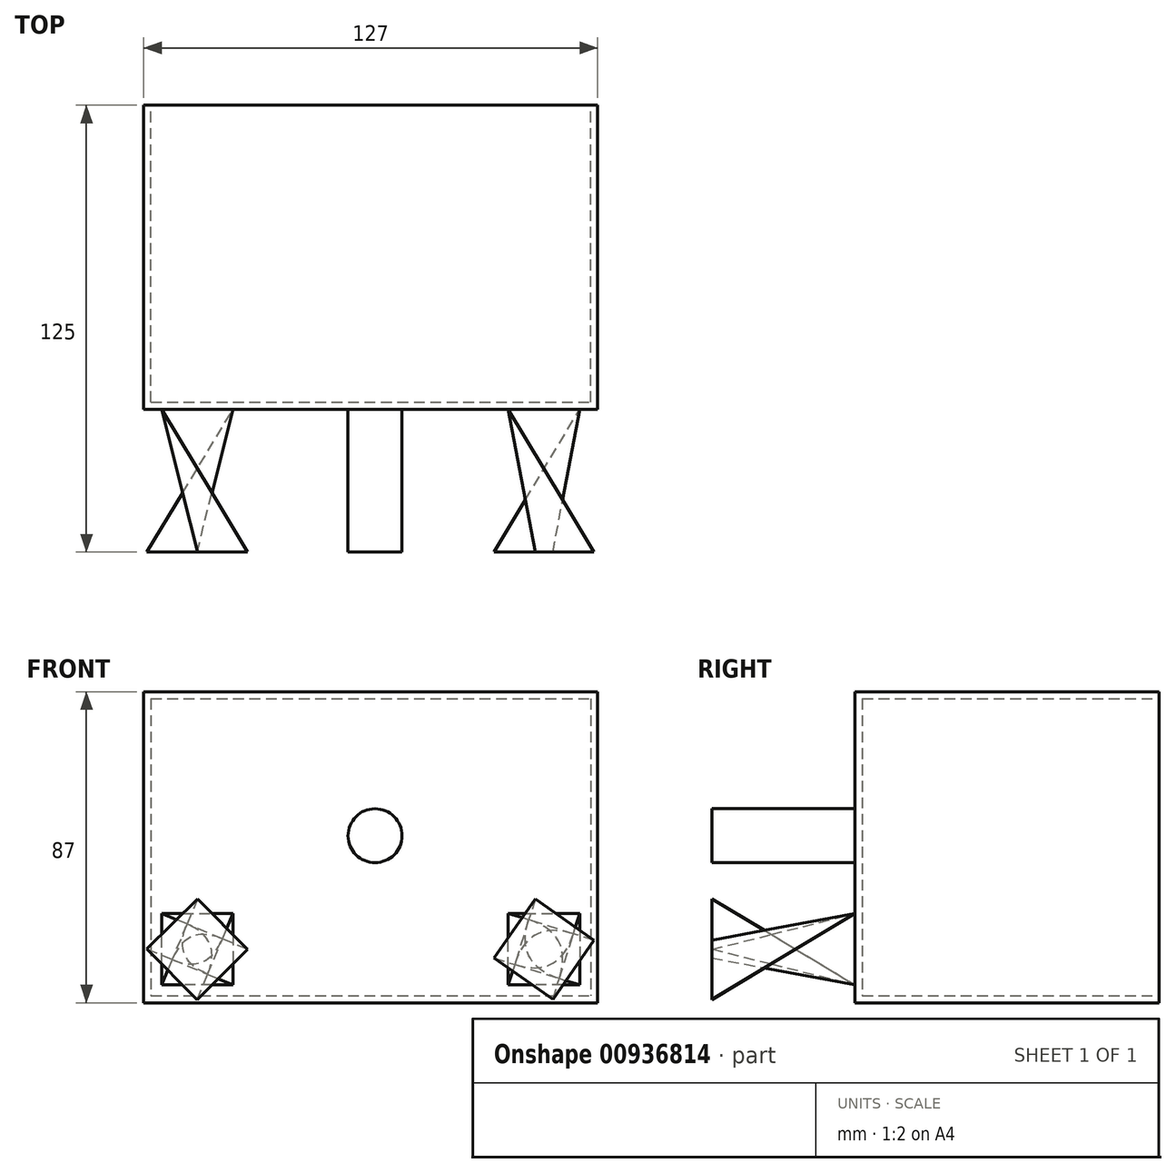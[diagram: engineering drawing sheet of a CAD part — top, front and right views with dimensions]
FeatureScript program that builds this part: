
annotation { "Feature Type Name" : "Feature", "Feature Type Description" : "" }
export const myFeature = defineFeature(function(context is Context, id is Id, definition is map)
    precondition{}
    {
        {
            var Q0;
            Q0=qCreatedBy(makeId("Front.planeOp"),FACE);
            var sketch = newSketch(context, id + "F0", { "sketchPlane" : qUnion([Q0])});
            skLineSegment(sketch, "E0.bottom", {"start": v(-53.91, 27.97) * mm, "end": v(73.09, 27.97) * mm});
            skLineSegment(sketch, "E0.top", {"start": v(-53.91, -59.03) * mm, "end": v(73.09, -59.03) * mm});
            skLineSegment(sketch, "E0.left", {"start": v(-53.91, 27.97) * mm, "end": v(-53.91, -59.03) * mm});
            skLineSegment(sketch, "E0.right", {"start": v(73.09, 27.97) * mm, "end": v(73.09, -59.03) * mm});
            skSolve(sketch);
        }
        {
            var Q0;
            Q0 = qSketchRegion(id + "F0", true);
            extrude(context, id + "F1", {"entities" : qUnion([Q0]), "depth" : 85 * mm, "offsetDistance" : 25 * mm});
        }
        {
            var Q0;
            Q0=makeQuery(id+"F1.opExtrude","CAP_FACE",FACE,{"disambiguationData":[OSD([sQuery(id+"F0.wireOp",EDGE,"E0.bottom"),sQuery(id+"F0.wireOp",EDGE,"E0.top"),sQuery(id+"F0.wireOp",EDGE,"E0.left"),sQuery(id+"F0.wireOp",EDGE,"E0.right")])],"isStart":true});
            shell(context, id + "F2", {"entities" : qUnion([Q0]), "thickness" : 2 * mm});
        }
        {
            var Q0;
            Q0=makeQuery(id+"F1.opExtrude","CAP_FACE",FACE,{"disambiguationData":[OSD([sQuery(id+"F0.wireOp",EDGE,"E0.bottom"),sQuery(id+"F0.wireOp",EDGE,"E0.top"),sQuery(id+"F0.wireOp",EDGE,"E0.left"),sQuery(id+"F0.wireOp",EDGE,"E0.right")])],"isStart":false});
            var sketch = newSketch(context, id + "F3", { "sketchPlane" : qUnion([Q0])});
            skCircle(sketch, "E1.cCircle", {"center": v(58.09, -44.03) * mm, "radius": 10 * mm, "construction": true});
            skLineSegment(sketch, "E1.0", {"start": v(68.09, -34.03) * mm, "end": v(68.09, -54.03) * mm});
            skLineSegment(sketch, "E1.1", {"start": v(68.09, -54.03) * mm, "end": v(48.09, -54.03) * mm});
            skLineSegment(sketch, "E1.2", {"start": v(48.09, -54.03) * mm, "end": v(48.09, -34.03) * mm});
            skLineSegment(sketch, "E1.3", {"start": v(48.09, -34.03) * mm, "end": v(68.09, -34.03) * mm});
            skPoint(sketch, "E1.0.midPoint", {"position": v(68.09, -44.03) * mm});
            skCircle(sketch, "E2.cCircle", {"center": v(-38.91, -44.03) * mm, "radius": 10 * mm, "construction": true});
            skLineSegment(sketch, "E2.0", {"start": v(-28.91, -54.03) * mm, "end": v(-48.91, -54.03) * mm});
            skLineSegment(sketch, "E2.1", {"start": v(-48.91, -54.03) * mm, "end": v(-48.91, -34.03) * mm});
            skLineSegment(sketch, "E2.2", {"start": v(-48.91, -34.03) * mm, "end": v(-28.91, -34.03) * mm});
            skLineSegment(sketch, "E2.3", {"start": v(-28.91, -34.03) * mm, "end": v(-28.91, -54.03) * mm});
            skPoint(sketch, "E2.0.midPoint", {"position": v(-38.91, -54.03) * mm});
            skCircle(sketch, "E3", {"center": v(10.8, -12.31) * mm, "radius": 7.55 * mm});
            skSolve(sketch);
        }
        {
            var Q0;
            Q0=makeQuery(id+"F3.imprint","IMPRINT",FACE,{"disambiguationData":[TD([[makeQuery(id+"F3.imprint","IMPRINT",EDGE,{"derivedFrom":sQuery(id+"F3.wireOp",EDGE,"E3")}),1.0]])]});
            extrude(context, id + "F4", {"entities" : qUnion([Q0]), "operationType" : NewBodyOperationType.ADD, "depth" : 40 * mm, "offsetDistance" : 25 * mm});
        }
        {
            var Q0;
            Q0=makeQuery(id+"F4.opExtrude","CAP_FACE",FACE,{"disambiguationData":[OSD([sQuery(id+"F3.wireOp",EDGE,"E3")])],"isStart":false});
            var sketch = newSketch(context, id + "F5", { "sketchPlane" : qUnion([Q0])});
            skCircle(sketch, "E4.cCircle", {"center": v(58.09, -44.03) * mm, "radius": 10.05 * mm, "construction": true});
            skLineSegment(sketch, "E4.0", {"start": v(72.09, -41.56) * mm, "end": v(60.56, -58.03) * mm});
            skLineSegment(sketch, "E4.1", {"start": v(60.56, -58.03) * mm, "end": v(44.09, -46.5) * mm});
            skLineSegment(sketch, "E4.2", {"start": v(44.09, -46.5) * mm, "end": v(55.62, -30.03) * mm});
            skLineSegment(sketch, "E4.3", {"start": v(55.62, -30.03) * mm, "end": v(72.09, -41.56) * mm});
            skPoint(sketch, "E4.0.midPoint", {"position": v(66.32, -49.8) * mm});
            skCircle(sketch, "E5.cCircle", {"center": v(-38.93, -44.05) * mm, "radius": 9.96 * mm, "construction": true});
            skLineSegment(sketch, "E5.0", {"start": v(-24.84, -44.11) * mm, "end": v(-38.99, -58.14) * mm});
            skLineSegment(sketch, "E5.1", {"start": v(-38.99, -58.14) * mm, "end": v(-53.01, -43.99) * mm});
            skLineSegment(sketch, "E5.2", {"start": v(-53.01, -43.99) * mm, "end": v(-38.86, -29.97) * mm});
            skLineSegment(sketch, "E5.3", {"start": v(-38.86, -29.97) * mm, "end": v(-24.84, -44.11) * mm});
            skPoint(sketch, "E5.0.midPoint", {"position": v(-31.91, -51.13) * mm});
            skSolve(sketch);
        }
        {
            var Q1;
            Q1=makeQuery(id+"F5.imprint","IMPRINT",FACE,{"disambiguationData":[TD([[makeQuery(id+"F5.imprint","IMPRINT",EDGE,{"derivedFrom":sQuery(id+"F5.wireOp",EDGE,"E4.0")}),-1.0]])]});
            var Q2;
            Q2=makeQuery(id+"F3.imprint","IMPRINT",FACE,{"disambiguationData":[TD([[makeQuery(id+"F3.imprint","IMPRINT",EDGE,{"derivedFrom":sQuery(id+"F3.wireOp",EDGE,"E1.0")}),-1.0]])]});
            var Q3;
            Q3=sQuery(id+"F3.wireOp",VERTEX,"E1.1.end");
            var Q4;
            Q4=sQuery(id+"F5.wireOp",VERTEX,"E4.2.end");
            loft(context, id + "F6", {"operationType" : NewBodyOperationType.ADD, "sheetProfilesArray" : [{ "sheetProfileEntities" : qUnion([Q1]) }, { "sheetProfileEntities" : qUnion([Q2]) }], "matchConnections" : true, "connections" : [{ "connectionEntities" : qUnion([Q3, Q4]), "connectionEdgeQueries" : qUnion([]), "connectionEdgeParameters" : [] }]});
        }
        {
            var Q1;
            Q1=makeQuery(id+"F5.imprint","IMPRINT",FACE,{"disambiguationData":[TD([[makeQuery(id+"F5.imprint","IMPRINT",EDGE,{"derivedFrom":sQuery(id+"F5.wireOp",EDGE,"E5.0")}),-1.0]])]});
            var Q2;
            Q2=makeQuery(id+"F3.imprint","IMPRINT",FACE,{"disambiguationData":[TD([[makeQuery(id+"F3.imprint","IMPRINT",EDGE,{"derivedFrom":sQuery(id+"F3.wireOp",EDGE,"E2.0")}),-1.0]])]});
            var Q3;
            Q3=sQuery(id+"F3.wireOp",VERTEX,"E2.0.end");
            var Q4;
            Q4=sQuery(id+"F5.wireOp",VERTEX,"E5.2.end");
            loft(context, id + "F7", {"operationType" : NewBodyOperationType.ADD, "sheetProfilesArray" : [{ "sheetProfileEntities" : qUnion([Q1]) }, { "sheetProfileEntities" : qUnion([Q2]) }], "matchConnections" : true, "connections" : [{ "connectionEntities" : qUnion([Q3, Q4]), "connectionEdgeQueries" : qUnion([]), "connectionEdgeParameters" : [] }]});
        }
    });
